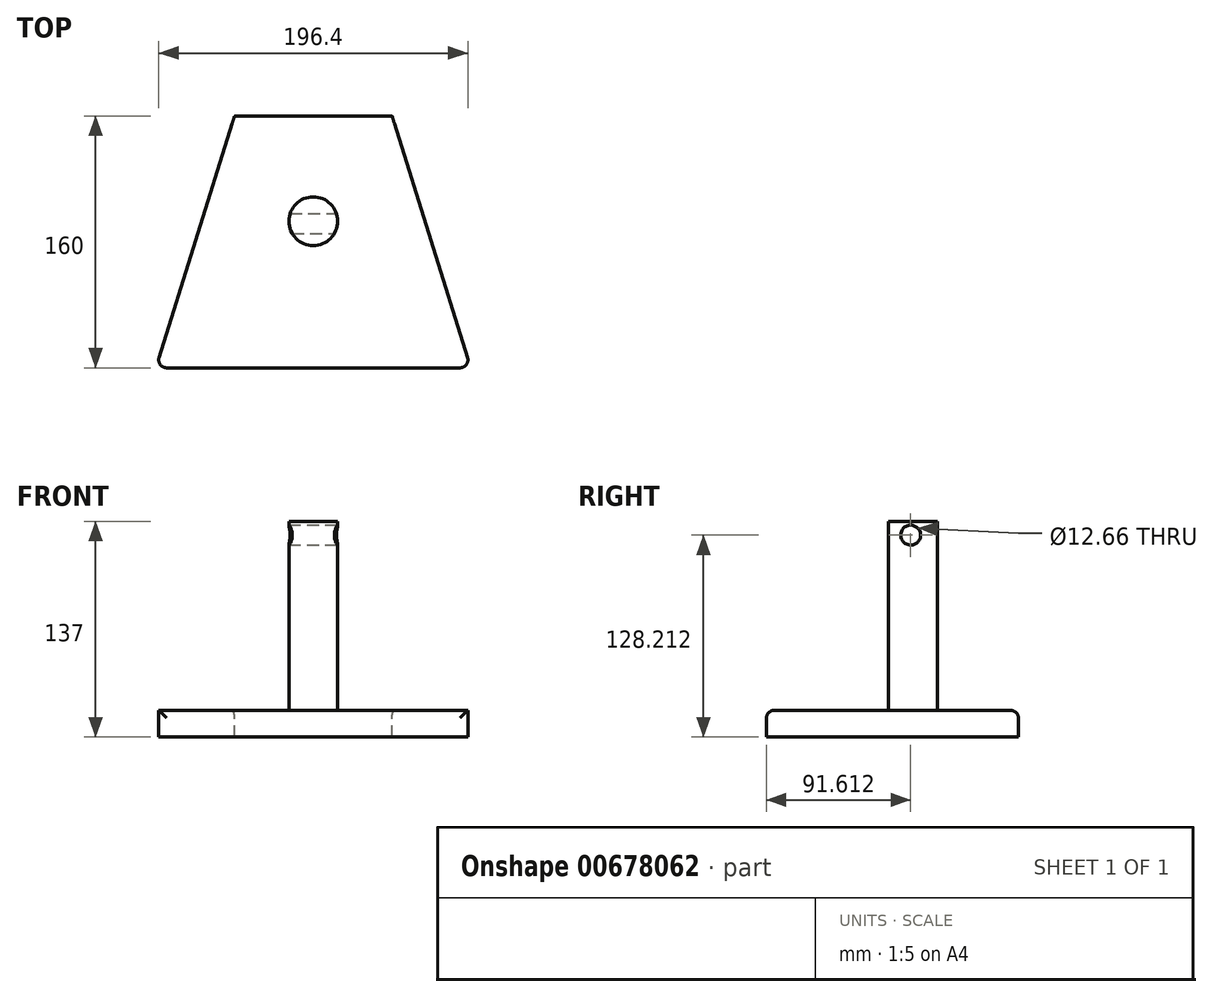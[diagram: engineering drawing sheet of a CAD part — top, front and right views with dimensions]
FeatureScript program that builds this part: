
annotation { "Feature Type Name" : "Feature", "Feature Type Description" : "" }
export const myFeature = defineFeature(function(context is Context, id is Id, definition is map)
    precondition{}
    {
        {
            var Q0;
            Q0=qCreatedBy(makeId("Top.planeOp"),FACE);
            var sketch = newSketch(context, id + "F0", { "sketchPlane" : qUnion([Q0])});
            skLineSegment(sketch, "E0.bottom", {"start": v(-94.38, 94.26) * mm, "end": v(105.62, 94.26) * mm});
            skLineSegment(sketch, "E0.top", {"start": v(-94.38, -65.74) * mm, "end": v(105.62, -65.74) * mm});
            skLineSegment(sketch, "E0.left", {"start": v(-94.38, 94.26) * mm, "end": v(-94.38, -65.74) * mm});
            skLineSegment(sketch, "E0.right", {"start": v(105.62, 94.26) * mm, "end": v(105.62, -65.74) * mm});
            skSolve(sketch);
        }
        {
            var Q0;
            Q0=makeQuery(id+"F0.imprint","IMPRINT",FACE,{"disambiguationData":[TD([[makeQuery(id+"F0.imprint","IMPRINT",EDGE,{"derivedFrom":sQuery(id+"F0.wireOp",EDGE,"E0.bottom")}),-1.0]])]});
            extrude(context, id + "F1", {"entities" : qUnion([Q0]), "depth" : 17 * mm, "offsetDistance" : 25 * mm});
        }
        {
            var Q0;
            Q0=makeQuery(id+"F1.opExtrude","CAP_FACE",FACE,{"disambiguationData":[OSD([sQuery(id+"F0.wireOp",EDGE,"E0.bottom"),sQuery(id+"F0.wireOp",EDGE,"E0.top"),sQuery(id+"F0.wireOp",EDGE,"E0.left"),sQuery(id+"F0.wireOp",EDGE,"E0.right")])],"isStart":false});
            var sketch = newSketch(context, id + "F2", { "sketchPlane" : qUnion([Q0])});
            skLineSegment(sketch, "E1", {"start": v(-94.38, -65.74) * mm, "end": v(-44.38, 94.26) * mm});
            skLineSegment(sketch, "E2", {"start": v(105.62, -65.74) * mm, "end": v(55.62, 94.26) * mm});
            skSolve(sketch);
        }
        {
            var Q0;
            {var subQ0=sQuery(id+"F2.wireOp",EDGE,"E1");Q0=makeQuery(id+"F2.imprint","IMPRINT",FACE,{"disambiguationData":[TD([[makeQuery(id+"F2.imprint","IMPRINT",EDGE,{"derivedFrom":subQ0}),1.0]])]});}
            var Q1;
            {var subQ0=sQuery(id+"F2.wireOp",EDGE,"E2");Q1=makeQuery(id+"F2.imprint","IMPRINT",FACE,{"disambiguationData":[TD([[makeQuery(id+"F2.imprint","IMPRINT",EDGE,{"derivedFrom":subQ0}),-1.0]])]});}
            extrude(context, id + "F3", {"entities" : qUnion([Q0, Q1]), "operationType" : NewBodyOperationType.REMOVE, "endBound" : BoundingType.THROUGH_ALL, "oppositeDirection" : true, "depth" : 25 * mm, "offsetDistance" : 25 * mm});
        }
        {
            var Q0;
            {var subQ0=sQuery(id+"F0.wireOp",EDGE,"E0.left");var subQ1=sQuery(id+"F0.wireOp",EDGE,"E0.top");Q0=makeQuery(id+"F3.boolean.opBoolean","MERGE",EDGE,{"derivedFrom":[makeQuery(id+"F1.opExtrude","SWEPT_EDGE",EDGE,{"disambiguationData":[OSD([subQ1,subQ0])]}),makeQuery(id+"F3.opExtrude","SWEPT_EDGE",EDGE,{"disambiguationData":[OSD([subQ1,subQ0,sQuery(id+"F2.wireOp",EDGE,"E1")])]})]});}
            var Q1;
            {var subQ0=sQuery(id+"F0.wireOp",EDGE,"E0.right");var subQ1=sQuery(id+"F0.wireOp",EDGE,"E0.top");Q1=makeQuery(id+"F3.boolean.opBoolean","MERGE",EDGE,{"derivedFrom":[makeQuery(id+"F1.opExtrude","SWEPT_EDGE",EDGE,{"disambiguationData":[OSD([subQ1,subQ0])]}),makeQuery(id+"F3.opExtrude","SWEPT_EDGE",EDGE,{"disambiguationData":[OSD([subQ1,subQ0,sQuery(id+"F2.wireOp",EDGE,"E2")])]})]});}
            var Q2;
            Q2=makeQuery(id+"F3.boolean.opBoolean","COPY",EDGE,{"derivedFrom":makeQuery(id+"F3.opExtrude","SWEPT_EDGE",EDGE,{"disambiguationData":[OSD([sQuery(id+"F0.wireOp",EDGE,"E0.bottom"),sQuery(id+"F2.wireOp",EDGE,"E2")])]})});
            var Q3;
            Q3=makeQuery(id+"F3.boolean.opBoolean","COPY",EDGE,{"derivedFrom":makeQuery(id+"F3.opExtrude","SWEPT_EDGE",EDGE,{"disambiguationData":[OSD([sQuery(id+"F0.wireOp",EDGE,"E0.bottom"),sQuery(id+"F2.wireOp",EDGE,"E1")])]})});
            var Q4;
            Q4=makeQuery(id+"F3.boolean.opBoolean","COPY",EDGE,{"derivedFrom":makeQuery(id+"F3.opExtrude","CAP_EDGE",EDGE,{"disambiguationData":[OSD([sQuery(id+"F2.wireOp",EDGE,"E2")])],"isStart":true})});
            var Q5;
            Q5=makeQuery(id+"F1.opExtrude","CAP_EDGE",EDGE,{"disambiguationData":[OSD([sQuery(id+"F0.wireOp",EDGE,"E0.top")])],"isStart":false});
            var Q6;
            Q6=makeQuery(id+"F3.boolean.opBoolean","COPY",EDGE,{"derivedFrom":makeQuery(id+"F3.opExtrude","CAP_EDGE",EDGE,{"disambiguationData":[OSD([sQuery(id+"F2.wireOp",EDGE,"E1")])],"isStart":true})});
            var Q7;
            Q7=makeQuery(id+"F1.opExtrude","CAP_EDGE",EDGE,{"disambiguationData":[OSD([sQuery(id+"F0.wireOp",EDGE,"E0.bottom")])],"isStart":false});
            fillet(context, id + "F4", {"entities" : qUnion([Q0, Q1, Q2, Q3, Q4, Q5, Q6, Q7]), "radius" : 5 * mm, "tangentPropagation" : true, "allowEdgeOverflow" : false});
        }
        {
            var Q0;
            Q0=makeQuery(id+"F1.opExtrude","CAP_FACE",FACE,{"disambiguationData":[OSD([sQuery(id+"F0.wireOp",EDGE,"E0.bottom"),sQuery(id+"F0.wireOp",EDGE,"E0.top"),sQuery(id+"F0.wireOp",EDGE,"E0.left"),sQuery(id+"F0.wireOp",EDGE,"E0.right")])],"isStart":false});
            var sketch = newSketch(context, id + "F5", { "sketchPlane" : qUnion([Q0])});
            skCircle(sketch, "E3", {"center": v(5.62, 27.34) * mm, "radius": 15.5 * mm});
            skPoint(sketch, "E3.centerSnap0", {"position": v(5.62, 89.26) * mm});
            skSolve(sketch);
        }
        {
            var Q0;
            Q0=makeQuery(id+"F5.imprint","IMPRINT",FACE,{"disambiguationData":[TD([[makeQuery(id+"F5.imprint","IMPRINT",EDGE,{"derivedFrom":sQuery(id+"F5.wireOp",EDGE,"E3")}),1.0]])]});
            extrude(context, id + "F6", {"entities" : qUnion([Q0]), "operationType" : NewBodyOperationType.ADD, "depth" : 120 * mm, "offsetDistance" : 25 * mm});
        }
        {
            var Q0;
            Q0=qCreatedBy(makeId("Right.planeOp"),FACE);
            var sketch = newSketch(context, id + "F7", { "sketchPlane" : qUnion([Q0])});
            skCircle(sketch, "E4", {"center": v(25.87, 128.21) * mm, "radius": 6.33 * mm});
            skSolve(sketch);
        }
        {
            var Q0;
            Q0 = qSketchRegion(id + "F7", true);
            extrude(context, id + "F8", {"entities" : qUnion([Q0]), "operationType" : NewBodyOperationType.REMOVE, "endBound" : BoundingType.SYMMETRIC, "oppositeDirection" : true, "depth" : 83.2 * mm, "offsetDistance" : 25 * mm});
        }
    });
